# Revit family: Doors_Industrial_Overhead-Door-Corporation_ProStar-Rolling-Steel-Sheet-Doors-780CD_
name_source: partatom
category: Specialty Equipment
units: mm (PartAtom-declared; Revit-internal decimal feet)

## family parameters
Always vertical = Yes
Cut with Voids When Loaded = No
Host = Wall
OmniClass Number = 23.30.10.21.34
OmniClass Title = Industrial Doors
Part Type = Normal
Room Calculation Point = No
Round Connector Dimension = Use Diameter
Shared = No

## types (2) — shared parameters
Description = MODEL 780CD COMMERCIAL ROLLING SHEET DOOR
Finish Material = Metal - Overhead Door - Galvanized Steel
Manufacturer = Overhead Door Corporation
Model = 780CD
Product Guid = 8ccebe07-a271-479c-8dcb-95e84ee5aac9
Product Page URL = https://www.overheaddoor.com
Product data url = https://www.bimobject.com
Slat Height = 10"
URL = https://www.overheaddoor.com
Wall Closure = By host

## type names
- ‏​Manual push-up
- Chain Hoist
type visibility flags (boolean, named after types; folded from table):
- ‏​Manual push-up: Yes: (none)
- Chain Hoist: Yes: Chain Hoist

## geometry (parser evidence)
native form markers: Sweep x11
no freeform markers — native parametric forms only
